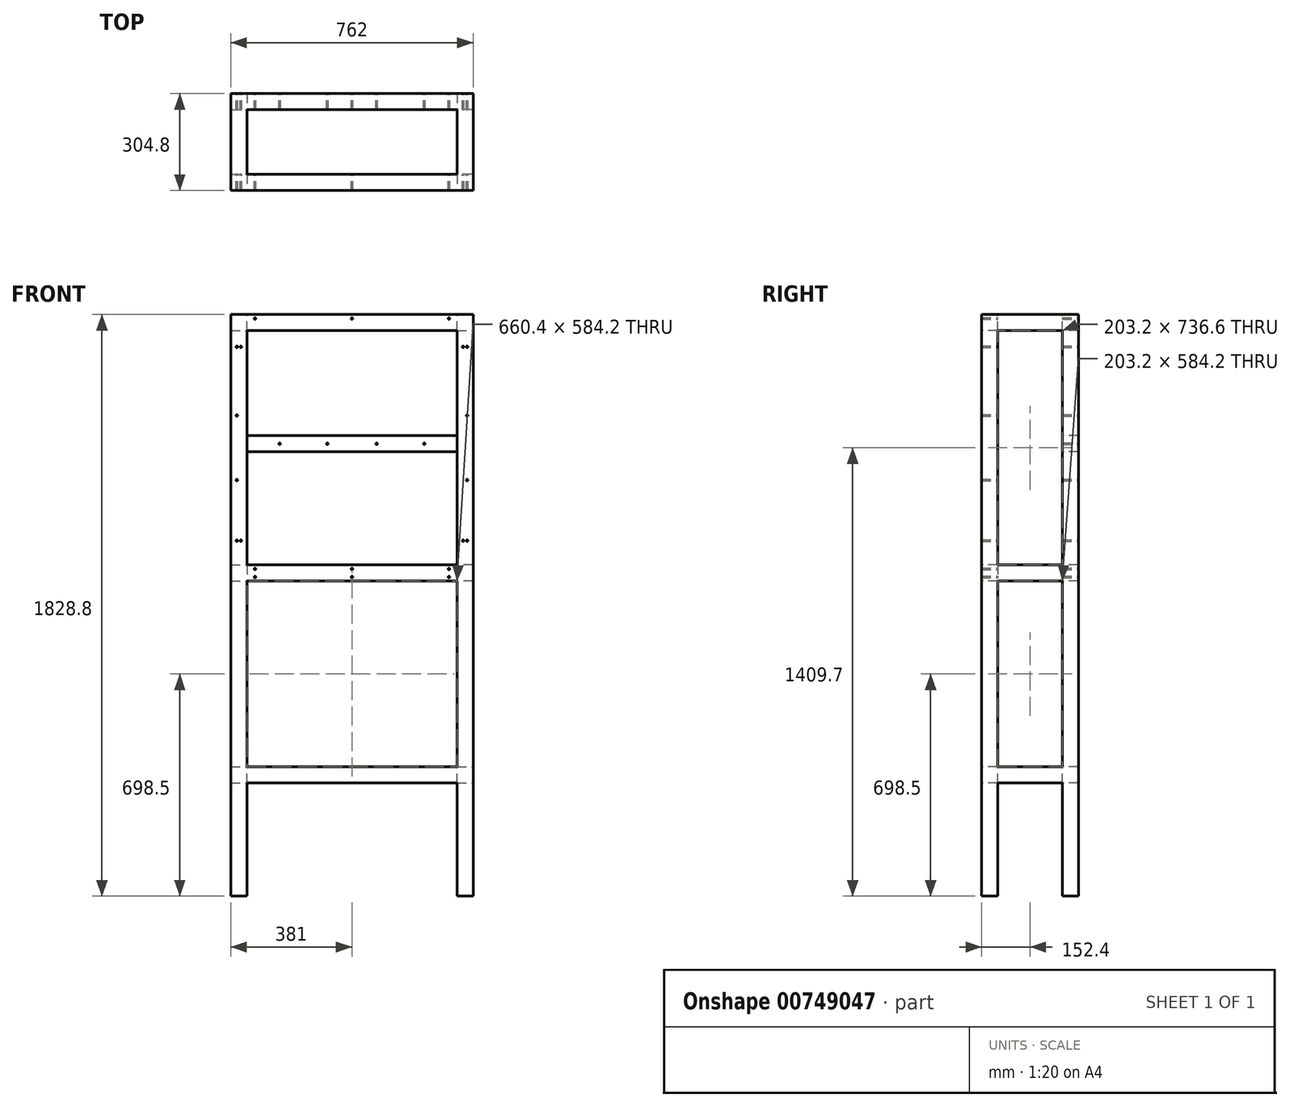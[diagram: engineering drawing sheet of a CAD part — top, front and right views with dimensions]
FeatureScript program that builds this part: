
annotation { "Feature Type Name" : "Feature", "Feature Type Description" : "" }
export const myFeature = defineFeature(function(context is Context, id is Id, definition is map)
    precondition{}
    {
        {
            var Q0;
            Q0=qCreatedBy(makeId("Front.planeOp"),FACE);
            var sketch = newSketch(context, id + "F0", { "sketchPlane" : qUnion([Q0])});
            skLineSegment(sketch, "E0.bottom", {"start": v(0, 0) * mm, "end": v(762, 0) * mm});
            skLineSegment(sketch, "E0.top", {"start": v(0, 1828.8) * mm, "end": v(762, 1828.8) * mm});
            skLineSegment(sketch, "E0.left", {"start": v(0, 0) * mm, "end": v(0, 1828.8) * mm});
            skLineSegment(sketch, "E0.right", {"start": v(762, 0) * mm, "end": v(762, 1828.8) * mm});
            skSolve(sketch);
        }
        {
            var Q0;
            Q0 = qSketchRegion(id + "F0", true);
            extrude(context, id + "F1", {"entities" : qUnion([Q0]), "depth" : 304.8 * mm, "offsetDistance" : 25.4 * mm});
        }
        {
            var Q0;
            Q0=makeQuery(id+"F1.opExtrude","SWEPT_FACE",FACE,{"disambiguationData":[OSD([sQuery(id+"F0.wireOp",EDGE,"E0.right")])]});
            var sketch = newSketch(context, id + "F2", { "sketchPlane" : qUnion([Q0])});
            skLineSegment(sketch, "E1.bottom", {"start": v(-254, 0) * mm, "end": v(-50.8, 0) * mm});
            skLineSegment(sketch, "E1.top", {"start": v(-254, 355.6) * mm, "end": v(-50.8, 355.6) * mm});
            skLineSegment(sketch, "E1.left", {"start": v(-254, 0) * mm, "end": v(-254, 355.6) * mm});
            skLineSegment(sketch, "E1.right", {"start": v(-50.8, 0) * mm, "end": v(-50.8, 355.6) * mm});
            skLineSegment(sketch, "E2.bottom", {"start": v(-254, 406.4) * mm, "end": v(-50.8, 406.4) * mm});
            skLineSegment(sketch, "E2.top", {"start": v(-254, 1778) * mm, "end": v(-50.8, 1778) * mm});
            skLineSegment(sketch, "E2.left", {"start": v(-254, 406.4) * mm, "end": v(-254, 1778) * mm});
            skLineSegment(sketch, "E2.right", {"start": v(-50.8, 406.4) * mm, "end": v(-50.8, 1778) * mm});
            skSolve(sketch);
        }
        {
            var Q0;
            Q0=makeQuery(id+"F2.imprint","IMPRINT",FACE,{"disambiguationData":[TD([[makeQuery(id+"F2.imprint","IMPRINT",EDGE,{"derivedFrom":sQuery(id+"F2.wireOp",EDGE,"E2.bottom")}),1.0]])]});
            var Q1;
            Q1=makeQuery(id+"F2.imprint","IMPRINT",FACE,{"disambiguationData":[TD([[makeQuery(id+"F2.imprint","IMPRINT",EDGE,{"derivedFrom":sQuery(id+"F2.wireOp",EDGE,"E1.bottom")}),1.0]])]});
            extrude(context, id + "F3", {"entities" : qUnion([Q0, Q1]), "operationType" : NewBodyOperationType.REMOVE, "oppositeDirection" : true, "depth" : 762 * mm, "offsetDistance" : 25.4 * mm});
        }
        {
            var Q0;
            Q0=makeQuery(id+"F1.opExtrude","CAP_FACE",FACE,{"disambiguationData":[OSD([sQuery(id+"F0.wireOp",EDGE,"E0.bottom"),sQuery(id+"F0.wireOp",EDGE,"E0.top"),sQuery(id+"F0.wireOp",EDGE,"E0.left"),sQuery(id+"F0.wireOp",EDGE,"E0.right")])],"isStart":false});
            var sketch = newSketch(context, id + "F4", { "sketchPlane" : qUnion([Q0])});
            skLineSegment(sketch, "E3.bottom", {"start": v(50.8, 0) * mm, "end": v(711.2, 0) * mm});
            skLineSegment(sketch, "E3.top", {"start": v(50.8, 355.6) * mm, "end": v(711.2, 355.6) * mm});
            skLineSegment(sketch, "E3.left", {"start": v(50.8, 0) * mm, "end": v(50.8, 355.6) * mm});
            skLineSegment(sketch, "E3.right", {"start": v(711.2, 0) * mm, "end": v(711.2, 355.6) * mm});
            skLineSegment(sketch, "E4.bottom", {"start": v(50.8, 406.4) * mm, "end": v(711.2, 406.4) * mm});
            skLineSegment(sketch, "E4.top", {"start": v(50.8, 990.6) * mm, "end": v(711.2, 990.6) * mm});
            skLineSegment(sketch, "E4.left", {"start": v(50.8, 406.4) * mm, "end": v(50.8, 990.6) * mm});
            skLineSegment(sketch, "E4.right", {"start": v(711.2, 406.4) * mm, "end": v(711.2, 990.6) * mm});
            skLineSegment(sketch, "E5.bottom", {"start": v(50.8, 1041.4) * mm, "end": v(711.2, 1041.4) * mm});
            skLineSegment(sketch, "E5.top", {"start": v(50.8, 1397) * mm, "end": v(711.2, 1397) * mm});
            skLineSegment(sketch, "E5.left", {"start": v(50.8, 1041.4) * mm, "end": v(50.8, 1397) * mm});
            skLineSegment(sketch, "E5.right", {"start": v(711.2, 1041.4) * mm, "end": v(711.2, 1397) * mm});
            skLineSegment(sketch, "E6.bottom", {"start": v(50.8, 1447.8) * mm, "end": v(711.2, 1447.8) * mm});
            skLineSegment(sketch, "E6.top", {"start": v(50.8, 1778) * mm, "end": v(711.2, 1778) * mm});
            skLineSegment(sketch, "E6.left", {"start": v(50.8, 1447.8) * mm, "end": v(50.8, 1778) * mm});
            skLineSegment(sketch, "E6.right", {"start": v(711.2, 1447.8) * mm, "end": v(711.2, 1778) * mm});
            skSolve(sketch);
        }
        {
            var Q0;
            Q0 = qSketchRegion(id + "F4", true);
            extrude(context, id + "F5", {"entities" : qUnion([Q0]), "operationType" : NewBodyOperationType.REMOVE, "oppositeDirection" : true, "depth" : 304.8 * mm, "offsetDistance" : 25.4 * mm});
        }
        {
            var Q0;
            Q0=makeQuery(id+"F1.opExtrude","SWEPT_FACE",FACE,{"disambiguationData":[OSD([sQuery(id+"F0.wireOp",EDGE,"E0.top")])]});
            var sketch = newSketch(context, id + "F6", { "sketchPlane" : qUnion([Q0])});
            skLineSegment(sketch, "E7.bottom", {"start": v(50.8, -50.8) * mm, "end": v(711.2, -50.8) * mm});
            skLineSegment(sketch, "E7.top", {"start": v(50.8, -254) * mm, "end": v(711.2, -254) * mm});
            skLineSegment(sketch, "E7.left", {"start": v(50.8, -50.8) * mm, "end": v(50.8, -254) * mm});
            skLineSegment(sketch, "E7.right", {"start": v(711.2, -50.8) * mm, "end": v(711.2, -254) * mm});
            skSolve(sketch);
        }
        {
            var Q0;
            Q0 = qSketchRegion(id + "F6", true);
            extrude(context, id + "F7", {"entities" : qUnion([Q0]), "operationType" : NewBodyOperationType.REMOVE, "oppositeDirection" : true, "depth" : 1524 * mm, "offsetDistance" : 25.4 * mm});
        }
        {
            var Q0;
            {var subQ3=sQuery(id+"F0.wireOp",EDGE,"E0.top");Q0=makeQuery(id+"F7.boolean.opBoolean","COPY",FACE,{"disambiguationData":[TD([makeQuery(id+"F1.opExtrude","SWEPT_FACE",FACE,{"disambiguationData":[OSD([subQ3])]})])],"derivedFrom":makeQuery(id+"F7.opExtrude","SWEPT_FACE",FACE,{"disambiguationData":[OSD([sQuery(id+"F6.wireOp",EDGE,"E7.bottom")])]})});}
            var sketch = newSketch(context, id + "F8", { "sketchPlane" : qUnion([Q0])});
            skPoint(sketch, "E8", {"position": v(76.2, 1816.1) * mm});
            skPoint(sketch, "E9", {"position": v(381, 1816.1) * mm});
            skPoint(sketch, "E10", {"position": v(685.8, 1816.1) * mm});
            skSolve(sketch);
        }
        {
            var Q0;
            Q0=sQuery(id+"F8.wireOp",VERTEX,"E8");
            var Q1;
            Q1=sQuery(id+"F8.wireOp",VERTEX,"E9");
            var Q2;
            Q2=sQuery(id+"F8.wireOp",VERTEX,"E10");
            var Q3;
            Q3=makeQuery(id+"F1.opExtrude","SWEPT_BODY",BODY,{"disambiguationData":[OSD([sQuery(id+"F0.wireOp",EDGE,"E0.bottom"),sQuery(id+"F0.wireOp",EDGE,"E0.top"),sQuery(id+"F0.wireOp",EDGE,"E0.left"),sQuery(id+"F0.wireOp",EDGE,"E0.right")])]});
            hole(context, id + "F9", {"style" : HoleStyle.SIMPLE, "endStyle" : HoleEndStyle.BLIND, "standardTappedOrClearance" : lookupTablePath({ "standard" : "ANSI", "engagement" : "75%", "pitch" : "20 tpi", "size" : "1/4", "type" : "Tapped" }), "standardBlindInLast" : lookupTablePath({ "standard" : "ANSI", "engagement" : "75%", "pitch" : "20 tpi", "size" : "1/4", "type" : "Tapped" }), "holeDiameter" : 5.1 * mm, "majorDiameter" : 6.35 * mm, "showTappedDepth" : true, "holeDepth" : 26.06 * mm, "isTappedThrough" : true, "tappedDepth" : 22.25 * mm, "tapClearance" : 3, "locations" : qUnion([Q0, Q1, Q2]), "scope" : qUnion([Q3])});
        }
        {
            var Q0;
            Q0=makeQuery(id+"F1.opExtrude","CAP_FACE",FACE,{"disambiguationData":[OSD([sQuery(id+"F0.wireOp",EDGE,"E0.bottom"),sQuery(id+"F0.wireOp",EDGE,"E0.top"),sQuery(id+"F0.wireOp",EDGE,"E0.left"),sQuery(id+"F0.wireOp",EDGE,"E0.right")])],"isStart":false});
            var sketch = newSketch(context, id + "F10", { "sketchPlane" : qUnion([Q0])});
            skLineSegment(sketch, "E11.bottom", {"start": v(50.8, 1447.8) * mm, "end": v(711.2, 1447.8) * mm});
            skLineSegment(sketch, "E11.top", {"start": v(50.8, 1397) * mm, "end": v(711.2, 1397) * mm});
            skLineSegment(sketch, "E11.left", {"start": v(50.8, 1447.8) * mm, "end": v(50.8, 1397) * mm});
            skLineSegment(sketch, "E11.right", {"start": v(711.2, 1447.8) * mm, "end": v(711.2, 1397) * mm});
            skSolve(sketch);
        }
        {
            var Q0;
            Q0 = qSketchRegion(id + "F10", true);
            extrude(context, id + "F11", {"entities" : qUnion([Q0]), "operationType" : NewBodyOperationType.REMOVE, "oppositeDirection" : true, "depth" : 50.8 * mm, "offsetDistance" : 25.4 * mm});
        }
        {
            var Q0;
            Q0=makeQuery(id+"F1.opExtrude","CAP_FACE",FACE,{"disambiguationData":[OSD([sQuery(id+"F0.wireOp",EDGE,"E0.bottom"),sQuery(id+"F0.wireOp",EDGE,"E0.top"),sQuery(id+"F0.wireOp",EDGE,"E0.left"),sQuery(id+"F0.wireOp",EDGE,"E0.right")])],"isStart":false});
            var sketch = newSketch(context, id + "F12", { "sketchPlane" : qUnion([Q0])});
            skLineSegment(sketch, "E12.bottom", {"start": v(711.2, 1041.4) * mm, "end": v(762, 1041.4) * mm});
            skLineSegment(sketch, "E12.top", {"start": v(711.2, 990.6) * mm, "end": v(762, 990.6) * mm});
            skLineSegment(sketch, "E12.left", {"start": v(711.2, 1041.4) * mm, "end": v(711.2, 990.6) * mm});
            skLineSegment(sketch, "E12.right", {"start": v(762, 1041.4) * mm, "end": v(762, 990.6) * mm});
            skLineSegment(sketch, "E13.bottom", {"start": v(50.8, 990.6) * mm, "end": v(0, 990.6) * mm});
            skLineSegment(sketch, "E13.top", {"start": v(50.8, 1041.4) * mm, "end": v(0, 1041.4) * mm});
            skLineSegment(sketch, "E13.left", {"start": v(50.8, 990.6) * mm, "end": v(50.8, 1041.4) * mm});
            skLineSegment(sketch, "E13.right", {"start": v(0, 990.6) * mm, "end": v(0, 1041.4) * mm});
            skSolve(sketch);
        }
        {
            var Q0;
            Q0 = qSketchRegion(id + "F12", true);
            extrude(context, id + "F13", {"entities" : qUnion([Q0]), "operationType" : NewBodyOperationType.ADD, "oppositeDirection" : true, "depth" : 304.8 * mm, "offsetDistance" : 25.4 * mm});
        }
        {
            var Q0;
            Q0=makeQuery(id+"F1.opExtrude","CAP_FACE",FACE,{"disambiguationData":[OSD([sQuery(id+"F0.wireOp",EDGE,"E0.bottom"),sQuery(id+"F0.wireOp",EDGE,"E0.top"),sQuery(id+"F0.wireOp",EDGE,"E0.left"),sQuery(id+"F0.wireOp",EDGE,"E0.right")])],"isStart":false});
            var sketch = newSketch(context, id + "F14", { "sketchPlane" : qUnion([Q0])});
            skLineSegment(sketch, "E14", {"start": v(381, 1828.8) * mm, "end": v(381, 990.6) * mm, "construction": true});
            skLineSegment(sketch, "E15", {"start": v(25.4, 1828.8) * mm, "end": v(25.4, 990.6) * mm, "construction": true});
            skLineSegment(sketch, "E16", {"start": v(0, 1422.4) * mm, "end": v(762, 1422.4) * mm, "construction": true});
            skPoint(sketch, "E17", {"position": v(19.05, 1727.2) * mm});
            skPoint(sketch, "E18", {"position": v(31.75, 1727.2) * mm});
            skPoint(sketch, "E19.MirrorP", {"position": v(19.05, 1117.6) * mm});
            skPoint(sketch, "E20.MirrorP", {"position": v(31.75, 1117.6) * mm});
            skPoint(sketch, "E21.MirrorP", {"position": v(730.25, 1727.2) * mm});
            skPoint(sketch, "E22.MirrorP", {"position": v(742.95, 1727.2) * mm});
            skPoint(sketch, "E23.MirrorP", {"position": v(742.95, 1117.6) * mm});
            skPoint(sketch, "E24.MirrorP", {"position": v(730.25, 1117.6) * mm});
            skSolve(sketch);
        }
        {
            var Q0;
            Q0=sQuery(id+"F14.wireOp",VERTEX,"E17");
            var Q1;
            Q1=sQuery(id+"F14.wireOp",VERTEX,"E18");
            var Q2;
            Q2=sQuery(id+"F14.wireOp",VERTEX,"E19.MirrorP");
            var Q3;
            Q3=sQuery(id+"F14.wireOp",VERTEX,"E20.MirrorP");
            var Q4;
            Q4=sQuery(id+"F14.wireOp",VERTEX,"E21.MirrorP");
            var Q5;
            Q5=sQuery(id+"F14.wireOp",VERTEX,"E22.MirrorP");
            var Q6;
            Q6=sQuery(id+"F14.wireOp",VERTEX,"E24.MirrorP");
            var Q7;
            Q7=sQuery(id+"F14.wireOp",VERTEX,"E23.MirrorP");
            var Q8;
            Q8=makeQuery(id+"F1.opExtrude","SWEPT_BODY",BODY,{"disambiguationData":[OSD([sQuery(id+"F0.wireOp",EDGE,"E0.bottom"),sQuery(id+"F0.wireOp",EDGE,"E0.top"),sQuery(id+"F0.wireOp",EDGE,"E0.left"),sQuery(id+"F0.wireOp",EDGE,"E0.right")])]});
            hole(context, id + "F15", {"style" : HoleStyle.SIMPLE, "endStyle" : HoleEndStyle.BLIND, "standardTappedOrClearance" : lookupTablePath({ "standard" : "ANSI", "engagement" : "75%", "pitch" : "20 tpi", "size" : "1/4", "type" : "Tapped" }), "standardBlindInLast" : lookupTablePath({ "standard" : "ANSI", "engagement" : "75%", "pitch" : "20 tpi", "size" : "1/4", "type" : "Tapped" }), "holeDiameter" : 5.1 * mm, "majorDiameter" : 6.35 * mm, "showTappedDepth" : true, "holeDepth" : 304.8 * mm, "isTappedThrough" : true, "tappedDepth" : 301 * mm, "tapClearance" : 3, "locations" : qUnion([Q0, Q1, Q2, Q3, Q4, Q5, Q6, Q7]), "scope" : qUnion([Q8])});
        }
        {
            var Q0;
            Q0=makeQuery(id+"F1.opExtrude","CAP_FACE",FACE,{"disambiguationData":[OSD([sQuery(id+"F0.wireOp",EDGE,"E0.bottom"),sQuery(id+"F0.wireOp",EDGE,"E0.top"),sQuery(id+"F0.wireOp",EDGE,"E0.left"),sQuery(id+"F0.wireOp",EDGE,"E0.right")])],"isStart":false});
            var sketch = newSketch(context, id + "F16", { "sketchPlane" : qUnion([Q0])});
            skLineSegment(sketch, "E25", {"start": v(0, 1409.7) * mm, "end": v(762, 1409.7) * mm, "construction": true});
            skPoint(sketch, "E25.startSnap0", {"position": v(50.8, 1409.7) * mm});
            skLineSegment(sketch, "E26", {"start": v(381, 1828.8) * mm, "end": v(381, 990.6) * mm, "construction": true});
            skLineSegment(sketch, "E27", {"start": v(742.95, 1828.8) * mm, "end": v(742.95, 990.6) * mm, "construction": true});
            skPoint(sketch, "E28", {"position": v(742.95, 1511.3) * mm});
            skPoint(sketch, "E29.MirrorP", {"position": v(742.95, 1308.1) * mm});
            skPoint(sketch, "E30.MirrorP", {"position": v(19.05, 1308.1) * mm});
            skPoint(sketch, "E31.MirrorP", {"position": v(19.05, 1511.3) * mm});
            skSolve(sketch);
        }
        {
            var Q0;
            Q0=sQuery(id+"F16.wireOp",VERTEX,"E31.MirrorP");
            var Q1;
            Q1=sQuery(id+"F16.wireOp",VERTEX,"E30.MirrorP");
            var Q2;
            Q2=sQuery(id+"F16.wireOp",VERTEX,"E28");
            var Q3;
            Q3=sQuery(id+"F16.wireOp",VERTEX,"E29.MirrorP");
            var Q4;
            Q4=makeQuery(id+"F1.opExtrude","SWEPT_BODY",BODY,{"disambiguationData":[OSD([sQuery(id+"F0.wireOp",EDGE,"E0.bottom"),sQuery(id+"F0.wireOp",EDGE,"E0.top"),sQuery(id+"F0.wireOp",EDGE,"E0.left"),sQuery(id+"F0.wireOp",EDGE,"E0.right")])]});
            hole(context, id + "F17", {"style" : HoleStyle.SIMPLE, "endStyle" : HoleEndStyle.BLIND, "standardTappedOrClearance" : lookupTablePath({ "standard" : "ANSI", "engagement" : "75%", "pitch" : "20 tpi", "size" : "1/4", "type" : "Tapped" }), "standardBlindInLast" : lookupTablePath({ "standard" : "ANSI", "engagement" : "75%", "pitch" : "20 tpi", "size" : "1/4", "type" : "Tapped" }), "holeDiameter" : 5.1 * mm, "majorDiameter" : 6.35 * mm, "showTappedDepth" : true, "holeDepth" : 304.8 * mm, "isTappedThrough" : true, "tappedDepth" : 301 * mm, "tapClearance" : 3, "locations" : qUnion([Q0, Q1, Q2, Q3]), "scope" : qUnion([Q4])});
        }
        {
            var Q0;
            Q0=makeQuery(id+"F1.opExtrude","CAP_FACE",FACE,{"disambiguationData":[OSD([sQuery(id+"F0.wireOp",EDGE,"E0.bottom"),sQuery(id+"F0.wireOp",EDGE,"E0.top"),sQuery(id+"F0.wireOp",EDGE,"E0.left"),sQuery(id+"F0.wireOp",EDGE,"E0.right")])],"isStart":false});
            var sketch = newSketch(context, id + "F18", { "sketchPlane" : qUnion([Q0])});
            skLineSegment(sketch, "E32", {"start": v(50.8, 1422.4) * mm, "end": v(711.2, 1422.4) * mm, "construction": true});
            skPoint(sketch, "E33", {"position": v(76.2, 1816.1) * mm});
            skPoint(sketch, "E34", {"position": v(381, 1816.1) * mm});
            skPoint(sketch, "E35", {"position": v(685.8, 1816.1) * mm});
            skLineSegment(sketch, "E36", {"start": v(0, 1816.1) * mm, "end": v(762, 1816.1) * mm, "construction": true});
            skPoint(sketch, "E37.MirrorP", {"position": v(76.2, 1028.7) * mm});
            skPoint(sketch, "E38.MirrorP", {"position": v(381, 1028.7) * mm});
            skPoint(sketch, "E39.MirrorP", {"position": v(685.8, 1028.7) * mm});
            skLineSegment(sketch, "E40", {"start": v(76.2, 1816.1) * mm, "end": v(303.5, 1422.4) * mm, "construction": true});
            skLineSegment(sketch, "E41", {"start": v(381, 1816.1) * mm, "end": v(608.3, 1422.4) * mm, "construction": true});
            skLineSegment(sketch, "E42", {"start": v(381, 1816.1) * mm, "end": v(153.7, 1422.4) * mm, "construction": true});
            skLineSegment(sketch, "E43", {"start": v(685.8, 1816.1) * mm, "end": v(458.5, 1422.4) * mm, "construction": true});
            skPoint(sketch, "E44", {"position": v(153.7, 1422.4) * mm});
            skPoint(sketch, "E45", {"position": v(303.5, 1422.4) * mm});
            skPoint(sketch, "E46", {"position": v(458.5, 1422.4) * mm});
            skPoint(sketch, "E47", {"position": v(608.3, 1422.4) * mm});
            skLineSegment(sketch, "E48", {"start": v(0, 1016) * mm, "end": v(762, 1016) * mm, "construction": true});
            skPoint(sketch, "E49.MirrorP", {"position": v(76.2, 1003.3) * mm});
            skPoint(sketch, "E50.MirrorP", {"position": v(381, 1003.3) * mm});
            skPoint(sketch, "E51.MirrorP", {"position": v(685.8, 1003.3) * mm});
            skSolve(sketch);
        }
        {
            var Q0;
            Q0=sQuery(id+"F18.wireOp",VERTEX,"E33");
            var Q1;
            Q1=sQuery(id+"F18.wireOp",VERTEX,"E41.start");
            var Q2;
            Q2=sQuery(id+"F18.wireOp",VERTEX,"E35");
            var Q3;
            Q3=sQuery(id+"F18.wireOp",VERTEX,"E41.end");
            var Q4;
            Q4=sQuery(id+"F18.wireOp",VERTEX,"E46");
            var Q5;
            Q5=sQuery(id+"F18.wireOp",VERTEX,"E45");
            var Q6;
            Q6=sQuery(id+"F18.wireOp",VERTEX,"E42.end");
            var Q7;
            Q7=sQuery(id+"F18.wireOp",VERTEX,"E37.MirrorP");
            var Q8;
            Q8=sQuery(id+"F18.wireOp",VERTEX,"E38.MirrorP");
            var Q9;
            Q9=sQuery(id+"F18.wireOp",VERTEX,"E39.MirrorP");
            var Q10;
            Q10=sQuery(id+"F18.wireOp",VERTEX,"E50.MirrorP");
            var Q11;
            Q11=sQuery(id+"F18.wireOp",VERTEX,"E49.MirrorP");
            var Q12;
            Q12=sQuery(id+"F18.wireOp",VERTEX,"E51.MirrorP");
            var Q13;
            Q13=makeQuery(id+"F1.opExtrude","SWEPT_BODY",BODY,{"disambiguationData":[OSD([sQuery(id+"F0.wireOp",EDGE,"E0.bottom"),sQuery(id+"F0.wireOp",EDGE,"E0.top"),sQuery(id+"F0.wireOp",EDGE,"E0.left"),sQuery(id+"F0.wireOp",EDGE,"E0.right")])]});
            hole(context, id + "F19", {"style" : HoleStyle.SIMPLE, "endStyle" : HoleEndStyle.BLIND, "standardTappedOrClearance" : lookupTablePath({ "standard" : "ANSI", "engagement" : "75%", "pitch" : "20 tpi", "size" : "1/4", "type" : "Tapped" }), "standardBlindInLast" : lookupTablePath({ "standard" : "ANSI", "engagement" : "75%", "pitch" : "20 tpi", "size" : "1/4", "type" : "Tapped" }), "holeDiameter" : 5.1 * mm, "majorDiameter" : 6.35 * mm, "showTappedDepth" : true, "holeDepth" : 304.8 * mm, "isTappedThrough" : true, "tappedDepth" : 301 * mm, "tapClearance" : 3, "locations" : qUnion([Q0, Q1, Q2, Q3, Q4, Q5, Q6, Q7, Q8, Q9, Q10, Q11, Q12]), "scope" : qUnion([Q13])});
        }
    });
